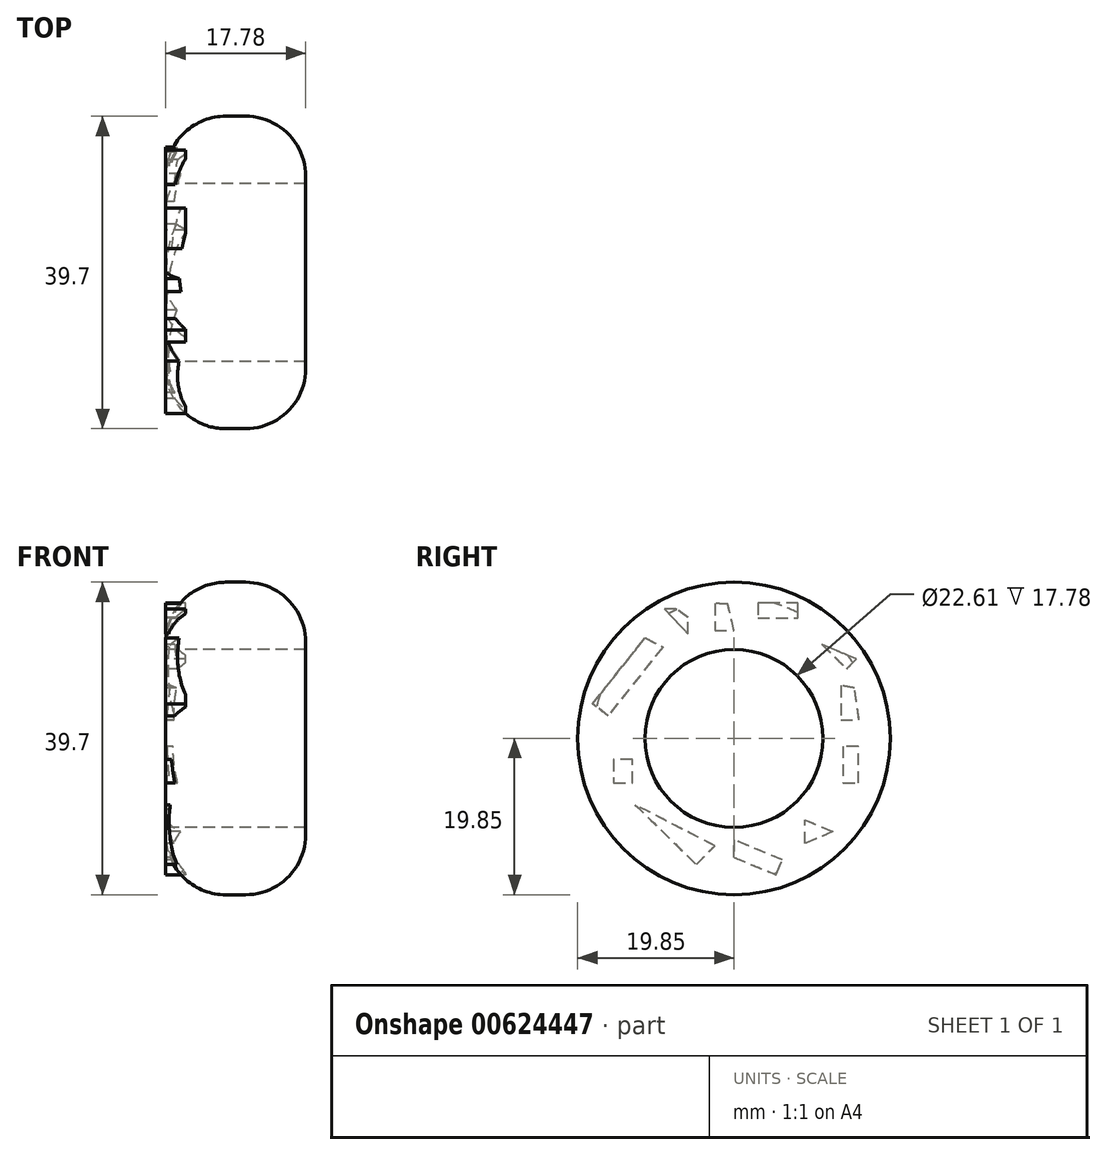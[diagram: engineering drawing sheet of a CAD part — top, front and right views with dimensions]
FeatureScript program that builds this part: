
annotation { "Feature Type Name" : "Feature", "Feature Type Description" : "" }
export const myFeature = defineFeature(function(context is Context, id is Id, definition is map)
    precondition{}
    {
        {
            var Q0;
            Q0=qCreatedBy(makeId("Right.planeOp"),FACE);
            var sketch = newSketch(context, id + "F0", { "sketchPlane" : qUnion([Q0])});
            skCircle(sketch, "E0", {"center": v(0, 0) * mm, "radius": 11.3 * mm});
            skCircle(sketch, "E1", {"center": v(0, 0) * mm, "radius": 19.85 * mm});
            skSolve(sketch);
        }
        {
            var Q0;
            Q0 = qSketchRegion(id + "F0", true);
            var Q1;
            Q1=makeQuery(id+"F0.imprint","IMPRINT",FACE,{"disambiguationData":[TD([[makeQuery(id+"F0.imprint","IMPRINT",EDGE,{"derivedFrom":sQuery(id+"F0.wireOp",EDGE,"E0")}),-1.0]])]});
            extrude(context, id + "F1", {"entities" : qUnion([Q0, Q1]), "depth" : 17.78 * mm, "offsetDistance" : 25.4 * mm});
        }
        {
            var Q0;
            Q0=makeQuery(id+"F1.opExtrude","CAP_EDGE",EDGE,{"disambiguationData":[OSD([sQuery(id+"F0.wireOp",EDGE,"E1")])],"isStart":false});
            var Q1;
            Q1=makeQuery(id+"F1.opExtrude","CAP_EDGE",EDGE,{"disambiguationData":[OSD([sQuery(id+"F0.wireOp",EDGE,"E1")])],"isStart":true});
            fillet(context, id + "F2", {"entities" : qUnion([Q0, Q1]), "radius" : 7.62 * mm, "tangentPropagation" : true, "allowEdgeOverflow" : false});
        }
        {
            var Q0;
            Q0=qCreatedBy(makeId("Right.planeOp"),FACE);
            var sketch = newSketch(context, id + "F3", { "sketchPlane" : qUnion([Q0])});
            skLineSegment(sketch, "E2", {"start": v(-12.56, -8.42) * mm, "end": v(-4.79, -16.03) * mm});
            skLineSegment(sketch, "E3", {"start": v(-4.79, -16.03) * mm, "end": v(-2.45, -13.63) * mm});
            skLineSegment(sketch, "E4", {"start": v(-2.45, -13.63) * mm, "end": v(-12.56, -8.42) * mm});
            skLineSegment(sketch, "E5", {"start": v(9, -13.34) * mm, "end": v(9, -10.33) * mm});
            skLineSegment(sketch, "E6", {"start": v(9, -10.33) * mm, "end": v(12.59, -11.84) * mm});
            skPoint(sketch, "E6.endSnap0", {"position": v(9, -11.84) * mm});
            skLineSegment(sketch, "E7", {"start": v(12.59, -11.84) * mm, "end": v(9, -13.34) * mm});
            skLineSegment(sketch, "E8", {"start": v(13.84, -0.98) * mm, "end": v(13.84, -5.68) * mm});
            skLineSegment(sketch, "E9", {"start": v(13.84, -5.68) * mm, "end": v(15.81, -5.68) * mm});
            skLineSegment(sketch, "E10", {"start": v(15.81, -5.68) * mm, "end": v(15.81, -0.98) * mm});
            skLineSegment(sketch, "E11", {"start": v(15.81, -0.98) * mm, "end": v(13.84, -0.98) * mm});
            skLineSegment(sketch, "E12", {"start": v(11.17, 11.95) * mm, "end": v(14.31, 8.83) * mm});
            skLineSegment(sketch, "E13", {"start": v(14.31, 8.83) * mm, "end": v(15.55, 10.08) * mm});
            skLineSegment(sketch, "E14", {"start": v(15.55, 10.08) * mm, "end": v(11.17, 11.95) * mm});
            skLineSegment(sketch, "E15", {"start": v(3.03, 15.3) * mm, "end": v(8.15, 15.3) * mm});
            skLineSegment(sketch, "E16", {"start": v(8.15, 15.3) * mm, "end": v(8.15, 17.2) * mm});
            skLineSegment(sketch, "E17", {"start": v(8.15, 17.2) * mm, "end": v(3.03, 17.2) * mm});
            skLineSegment(sketch, "E18", {"start": v(3.03, 17.2) * mm, "end": v(3.03, 15.3) * mm});
            skLineSegment(sketch, "E19", {"start": v(-2.43, 17.15) * mm, "end": v(-2.43, 13.7) * mm});
            skLineSegment(sketch, "E20", {"start": v(-2.43, 13.7) * mm, "end": v(0, 13.7) * mm});
            skLineSegment(sketch, "E21", {"start": v(0, 13.7) * mm, "end": v(-0.8, 17.06) * mm});
            skLineSegment(sketch, "E22", {"start": v(-0.8, 17.06) * mm, "end": v(-2.43, 17.15) * mm});
            skLineSegment(sketch, "E23", {"start": v(-9.05, 11.62) * mm, "end": v(-16, 2.86) * mm});
            skLineSegment(sketch, "E24", {"start": v(-16, 2.86) * mm, "end": v(-17.95, 4.4) * mm});
            skLineSegment(sketch, "E25", {"start": v(-17.95, 4.4) * mm, "end": v(-11.28, 12.8) * mm});
            skLineSegment(sketch, "E26", {"start": v(-11.28, 12.8) * mm, "end": v(-9.05, 11.62) * mm});
            skLineSegment(sketch, "E27", {"start": v(-15.28, -2.66) * mm, "end": v(-15.28, -5.67) * mm});
            skLineSegment(sketch, "E28", {"start": v(-15.28, -5.67) * mm, "end": v(-12.91, -5.67) * mm});
            skLineSegment(sketch, "E29", {"start": v(-12.91, -5.67) * mm, "end": v(-12.91, -2.66) * mm});
            skLineSegment(sketch, "E30", {"start": v(-12.91, -2.66) * mm, "end": v(-15.28, -2.66) * mm});
            skLineSegment(sketch, "E31", {"start": v(-8.86, 16.48) * mm, "end": v(-5.83, 13.29) * mm});
            skLineSegment(sketch, "E32", {"start": v(-5.83, 13.29) * mm, "end": v(-5.83, 15.35) * mm});
            skLineSegment(sketch, "E33", {"start": v(-5.83, 15.35) * mm, "end": v(-7.34, 16.48) * mm});
            skPoint(sketch, "E33.endSnap0", {"position": v(-7.34, 14.88) * mm});
            skLineSegment(sketch, "E34", {"start": v(-7.34, 16.48) * mm, "end": v(-8.86, 16.48) * mm});
            skLineSegment(sketch, "E35", {"start": v(0, -15.1) * mm, "end": v(5.35, -17.3) * mm});
            skLineSegment(sketch, "E36", {"start": v(5.35, -17.3) * mm, "end": v(6.14, -15.41) * mm});
            skLineSegment(sketch, "E37", {"start": v(6.14, -15.41) * mm, "end": v(0, -12.88) * mm});
            skLineSegment(sketch, "E38", {"start": v(0, -12.88) * mm, "end": v(0, -15.1) * mm});
            skLineSegment(sketch, "E39", {"start": v(13.56, 6.73) * mm, "end": v(13.56, 2.36) * mm});
            skLineSegment(sketch, "E40", {"start": v(13.56, 2.36) * mm, "end": v(15.9, 2.36) * mm});
            skLineSegment(sketch, "E41", {"start": v(15.9, 2.36) * mm, "end": v(15.3, 6.42) * mm});
            skLineSegment(sketch, "E42", {"start": v(15.3, 6.42) * mm, "end": v(13.56, 6.73) * mm});
            skSolve(sketch);
        }
        {
            var Q0;
            Q0=makeQuery(id+"F3.imprint","IMPRINT",FACE,{"disambiguationData":[TD([[makeQuery(id+"F3.imprint","IMPRINT",EDGE,{"derivedFrom":sQuery(id+"F3.wireOp",EDGE,"E23")}),-1.0]])]});
            var Q1;
            Q1=makeQuery(id+"F3.imprint","IMPRINT",FACE,{"disambiguationData":[TD([[makeQuery(id+"F3.imprint","IMPRINT",EDGE,{"derivedFrom":sQuery(id+"F3.wireOp",EDGE,"E31")}),1.0]])]});
            var Q2;
            Q2=makeQuery(id+"F3.imprint","IMPRINT",FACE,{"disambiguationData":[TD([[makeQuery(id+"F3.imprint","IMPRINT",EDGE,{"derivedFrom":sQuery(id+"F3.wireOp",EDGE,"E19")}),1.0]])]});
            var Q3;
            Q3=makeQuery(id+"F3.imprint","IMPRINT",FACE,{"disambiguationData":[TD([[makeQuery(id+"F3.imprint","IMPRINT",EDGE,{"derivedFrom":sQuery(id+"F3.wireOp",EDGE,"E15")}),1.0]])]});
            var Q4;
            Q4=makeQuery(id+"F3.imprint","IMPRINT",FACE,{"disambiguationData":[TD([[makeQuery(id+"F3.imprint","IMPRINT",EDGE,{"derivedFrom":sQuery(id+"F3.wireOp",EDGE,"E12")}),1.0]])]});
            var Q5;
            Q5=makeQuery(id+"F3.imprint","IMPRINT",FACE,{"disambiguationData":[TD([[makeQuery(id+"F3.imprint","IMPRINT",EDGE,{"derivedFrom":sQuery(id+"F3.wireOp",EDGE,"E39")}),1.0]])]});
            var Q6;
            Q6=makeQuery(id+"F3.imprint","IMPRINT",FACE,{"disambiguationData":[TD([[makeQuery(id+"F3.imprint","IMPRINT",EDGE,{"derivedFrom":sQuery(id+"F3.wireOp",EDGE,"E8")}),1.0]])]});
            var Q7;
            Q7=makeQuery(id+"F3.imprint","IMPRINT",FACE,{"disambiguationData":[TD([[makeQuery(id+"F3.imprint","IMPRINT",EDGE,{"derivedFrom":sQuery(id+"F3.wireOp",EDGE,"E5")}),-1.0]])]});
            var Q8;
            Q8=makeQuery(id+"F3.imprint","IMPRINT",FACE,{"disambiguationData":[TD([[makeQuery(id+"F3.imprint","IMPRINT",EDGE,{"derivedFrom":sQuery(id+"F3.wireOp",EDGE,"E35")}),1.0]])]});
            var Q9;
            Q9=makeQuery(id+"F3.imprint","IMPRINT",FACE,{"disambiguationData":[TD([[makeQuery(id+"F3.imprint","IMPRINT",EDGE,{"derivedFrom":sQuery(id+"F3.wireOp",EDGE,"E2")}),1.0]])]});
            var Q10;
            Q10=makeQuery(id+"F3.imprint","IMPRINT",FACE,{"disambiguationData":[TD([[makeQuery(id+"F3.imprint","IMPRINT",EDGE,{"derivedFrom":sQuery(id+"F3.wireOp",EDGE,"E27")}),1.0]])]});
            extrude(context, id + "F4", {"entities" : qUnion([Q0, Q1, Q2, Q3, Q4, Q5, Q6, Q7, Q8, Q9, Q10]), "operationType" : NewBodyOperationType.ADD, "depth" : 2.54 * mm, "offsetDistance" : 25.4 * mm});
        }
    });
